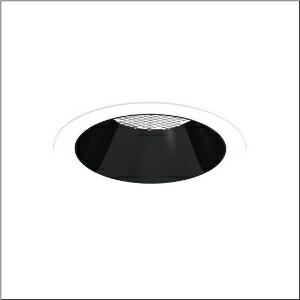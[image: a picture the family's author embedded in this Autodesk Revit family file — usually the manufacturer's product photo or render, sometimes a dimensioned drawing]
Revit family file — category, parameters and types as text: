
# Revit family: lunis_21_xl_51db17mf91c
name_source: partatom
category: Lighting Fixtures
units: mm (PartAtom-declared; Revit-internal decimal feet)

## family parameters
Cut with Voids When Loaded = No
Host = Face
Light Source = No
Part Type = Normal
Room Calculation Point = No
Round Connector Dimension = Use Diameter
Shared = No

## types (1)
- --- (1 x LED, 3170 lm, 21.7 W, 6500K)
    Apparent Load = 22 VA
    CIE Flux Codes = 92 100 100 100 100
    Color Rendering = 80
    Color Temperature = 6500K
    Default Elevation = 1800 mm
    Description = Lunis 21,  XL, downlight, light control with lens, of PMMA, anti glare with reflector, of PC, light emission: direct distribution, LED rated luminous flux: 2.120lm, light colour: 830/840/865, with terminal, 3-pole, mains connection: 220..240V, AC/DC, 0/50..60Hz, housing, round, of diecast aluminium, traffic white (RAL 9016), diameter: 230mm, clamping range: 1..40mm, protection rating (complete): IP20, protection rating (on room side): IP54, insulation class (complete): insulation class II (safety insulation), certification: CE, impact resistance: IK03, packaging unit: 1 piece
    Height = 0 mm  [stored 0 ft]
    Lamp = 1 x LED
    Lamp Light Flux = 3170 lm
    Lamp Power = 21.7 W
    Lamp count = 1
    Length = 230 mm
    Luminous efficacy = 146 lm/W
    Manufacturer = Siteco
    ModVariant = No
    Model = 51DB17MF91C
    Mounting Place = Ceiling
    Mounting Type = Recessed
    Number of Poles = 1
    OnlyDefault = Yes
    Power Factor = 1
    Product Name = Lunis 21 XL
    Product group = downlight
    ProductGroupID = 400
    Protection Class = Protection class II
    Protection Degree = IP 20
    RLX_Detail_Level = 1
    RLX_Emergency_Light_Flux = 0 lm
    RLX_Emergency_Type = 0
    RLX_Emergency_Type_DB = No
    RlxData = <blob elided: 20397 chars, md5=8022b9de>
    Socket = socket
    Standby Power = 0 W
    System Light Flux = 3170 lm
    System Power = 22 W
    Type Comments = individual setting: colour temperature 6500K, luminous flux: 100 % | (OFF | ON | ON | ON) | 650 mA
    Type Image = l_1291161.jpg
    URL = http://relux.com
    VarID = @adj_019828
    Voltage = 0 V
    Weight = 0.00 kg
    Width = 0 mm  [stored 0 ft]

note: [stored X ft] marks values corroborated as IEEE doubles in the binary element streams (Revit-internal decimal feet)

## geometry (parser evidence)
native form markers: Blend x4, Sweep x12
no freeform markers — native parametric forms only
